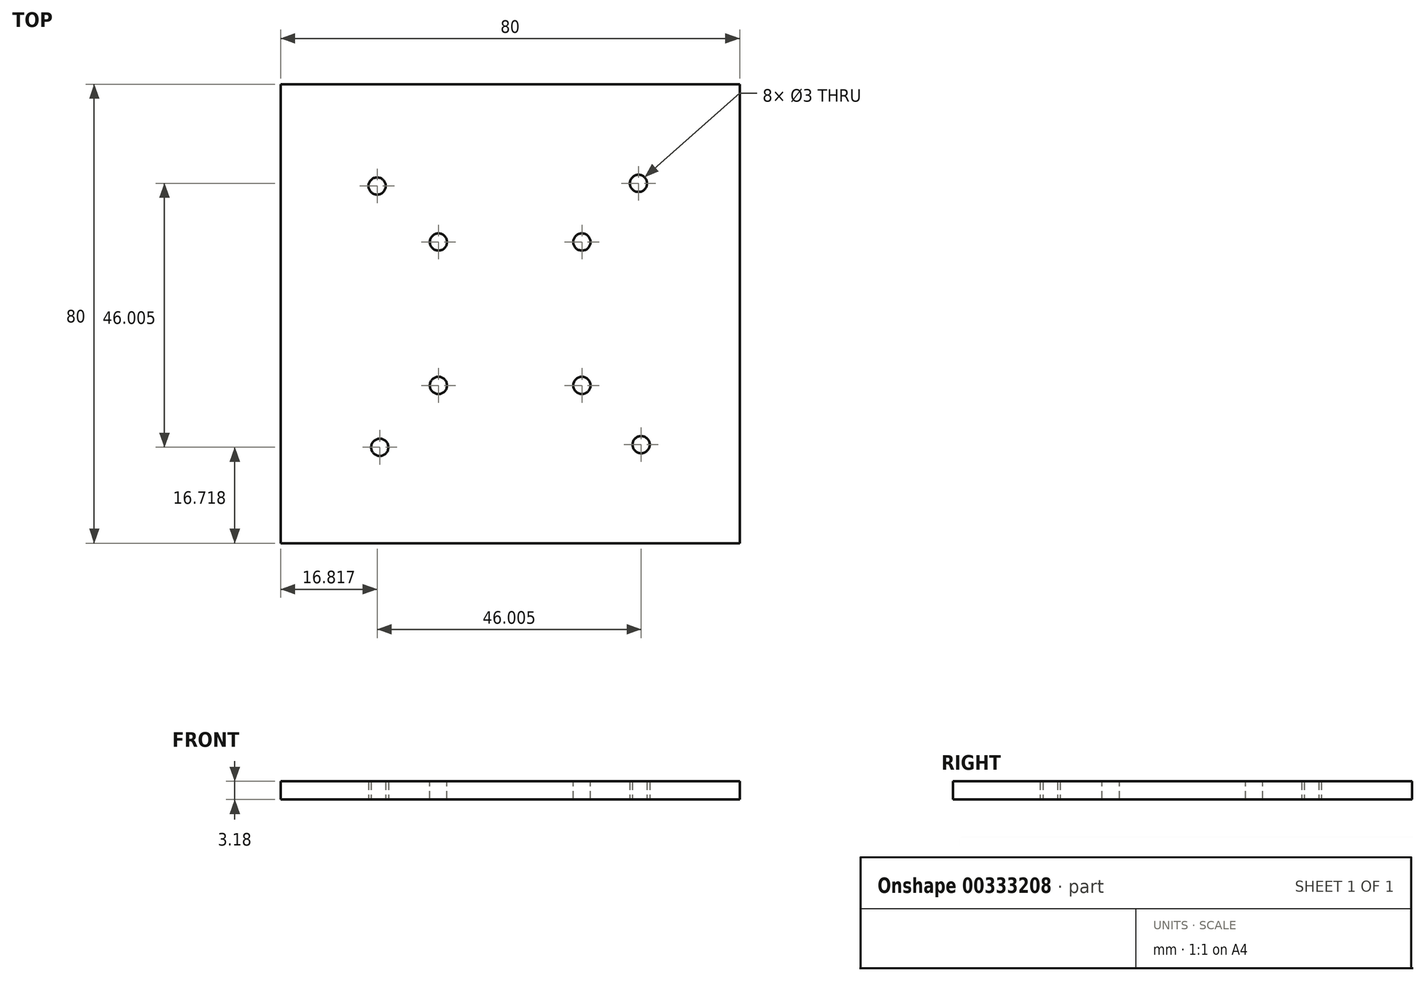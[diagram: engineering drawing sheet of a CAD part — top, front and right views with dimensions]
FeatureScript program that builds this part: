
annotation { "Feature Type Name" : "Feature", "Feature Type Description" : "" }
export const myFeature = defineFeature(function(context is Context, id is Id, definition is map)
    precondition{}
    {
        {
            var Q0;
            Q0=qCreatedBy(makeId("Top.planeOp"),FACE);
            var sketch = newSketch(context, id + "F0", { "sketchPlane" : qUnion([Q0])});
            skLineSegment(sketch, "E0.bottom", {"start": v(40, -40) * mm, "end": v(-40, -40) * mm});
            skLineSegment(sketch, "E0.top", {"start": v(40, 40) * mm, "end": v(-40, 40) * mm});
            skLineSegment(sketch, "E0.left", {"start": v(40, -40) * mm, "end": v(40, 40) * mm});
            skLineSegment(sketch, "E0.right", {"start": v(-40, -40) * mm, "end": v(-40, 40) * mm});
            skCircle(sketch, "E1", {"center": v(-23.18, 22.26) * mm, "radius": 1.5 * mm});
            skCircle(sketch, "E2.1.0", {"center": v(-22.72, -23.28) * mm, "radius": 1.5 * mm});
            skCircle(sketch, "E2.2.0", {"center": v(22.82, -22.82) * mm, "radius": 1.5 * mm});
            skCircle(sketch, "E2.3.0", {"center": v(22.36, 22.72) * mm, "radius": 1.5 * mm});
            skPoint(sketch, "E2.center", {"position": v(-0.18, -0.28) * mm});
            skSolve(sketch);
        }
        {
            var Q0;
            Q0=qSketchRegion(id+"F0",true);
            extrude(context, id + "F1", {"entities" : qUnion([Q0]), "depth" : 3.17 * mm});
        }
        {
            var Q0;
            Q0=makeQuery(id+"F1.opExtrude","CAP_FACE",FACE,{"disambiguationData":[OSD([sQuery(id+"F0.wireOp",EDGE,"E0.bottom"),sQuery(id+"F0.wireOp",EDGE,"E0.top"),sQuery(id+"F0.wireOp",EDGE,"E0.left"),sQuery(id+"F0.wireOp",EDGE,"E0.right"),sQuery(id+"F0.wireOp",EDGE,"E1"),sQuery(id+"F0.wireOp",EDGE,"E2.1.0"),sQuery(id+"F0.wireOp",EDGE,"E2.2.0"),sQuery(id+"F0.wireOp",EDGE,"E2.3.0")])],"isStart":false});
            var sketch = newSketch(context, id + "F2", { "sketchPlane" : qUnion([Q0])});
            skCircle(sketch, "E3.cCircle", {"center": v(0, 0) * mm, "radius": 17.68 * mm, "construction": true});
            skLineSegment(sketch, "E3.0", {"start": v(12.5, -12.5) * mm, "end": v(-12.5, -12.5) * mm, "construction": true});
            skLineSegment(sketch, "E3.1", {"start": v(-12.5, -12.5) * mm, "end": v(-12.5, 12.5) * mm, "construction": true});
            skLineSegment(sketch, "E3.2", {"start": v(-12.5, 12.5) * mm, "end": v(12.5, 12.5) * mm, "construction": true});
            skLineSegment(sketch, "E3.3", {"start": v(12.5, 12.5) * mm, "end": v(12.5, -12.5) * mm, "construction": true});
            skCircle(sketch, "E4", {"center": v(-12.5, 12.5) * mm, "radius": 1.5 * mm});
            skCircle(sketch, "E5.1.0", {"center": v(-12.5, -12.5) * mm, "radius": 1.5 * mm});
            skCircle(sketch, "E5.2.0", {"center": v(12.5, -12.5) * mm, "radius": 1.5 * mm});
            skCircle(sketch, "E5.3.0", {"center": v(12.5, 12.5) * mm, "radius": 1.5 * mm});
            skSolve(sketch);
        }
        {
            var Q0;
            Q0=makeQuery(id+"F2.imprint","IMPRINT",FACE,{"disambiguationData":[TD([[makeQuery(id+"F2.imprint","IMPRINT",EDGE,{"derivedFrom":sQuery(id+"F2.wireOp",EDGE,"E4")}),1.0]])]});
            var Q1;
            Q1=makeQuery(id+"F2.imprint","IMPRINT",FACE,{"disambiguationData":[TD([[makeQuery(id+"F2.imprint","IMPRINT",EDGE,{"derivedFrom":sQuery(id+"F2.wireOp",EDGE,"E5.3.0")}),1.0]])]});
            var Q2;
            Q2=makeQuery(id+"F2.imprint","IMPRINT",FACE,{"disambiguationData":[TD([[makeQuery(id+"F2.imprint","IMPRINT",EDGE,{"derivedFrom":sQuery(id+"F2.wireOp",EDGE,"E5.2.0")}),1.0]])]});
            var Q3;
            Q3=makeQuery(id+"F2.imprint","IMPRINT",FACE,{"disambiguationData":[TD([[makeQuery(id+"F2.imprint","IMPRINT",EDGE,{"derivedFrom":sQuery(id+"F2.wireOp",EDGE,"E5.1.0")}),1.0]])]});
            var Q4;
            Q4=sQuery(id+"F2.wireOp",EDGE,"E4");
            var Q5;
            Q5=sQuery(id+"F2.wireOp",EDGE,"E5.3.0");
            var Q6;
            Q6=sQuery(id+"F2.wireOp",EDGE,"E5.2.0");
            var Q7;
            Q7=sQuery(id+"F2.wireOp",EDGE,"E5.1.0");
            extrude(context, id + "F3", {"entities" : qUnion([Q0, Q1, Q2, Q3]), "operationType" : NewBodyOperationType.REMOVE, "surfaceEntities" : qUnion([Q4, Q5, Q6, Q7]), "oppositeDirection" : true, "depth" : 25 * mm});
        }
    });
